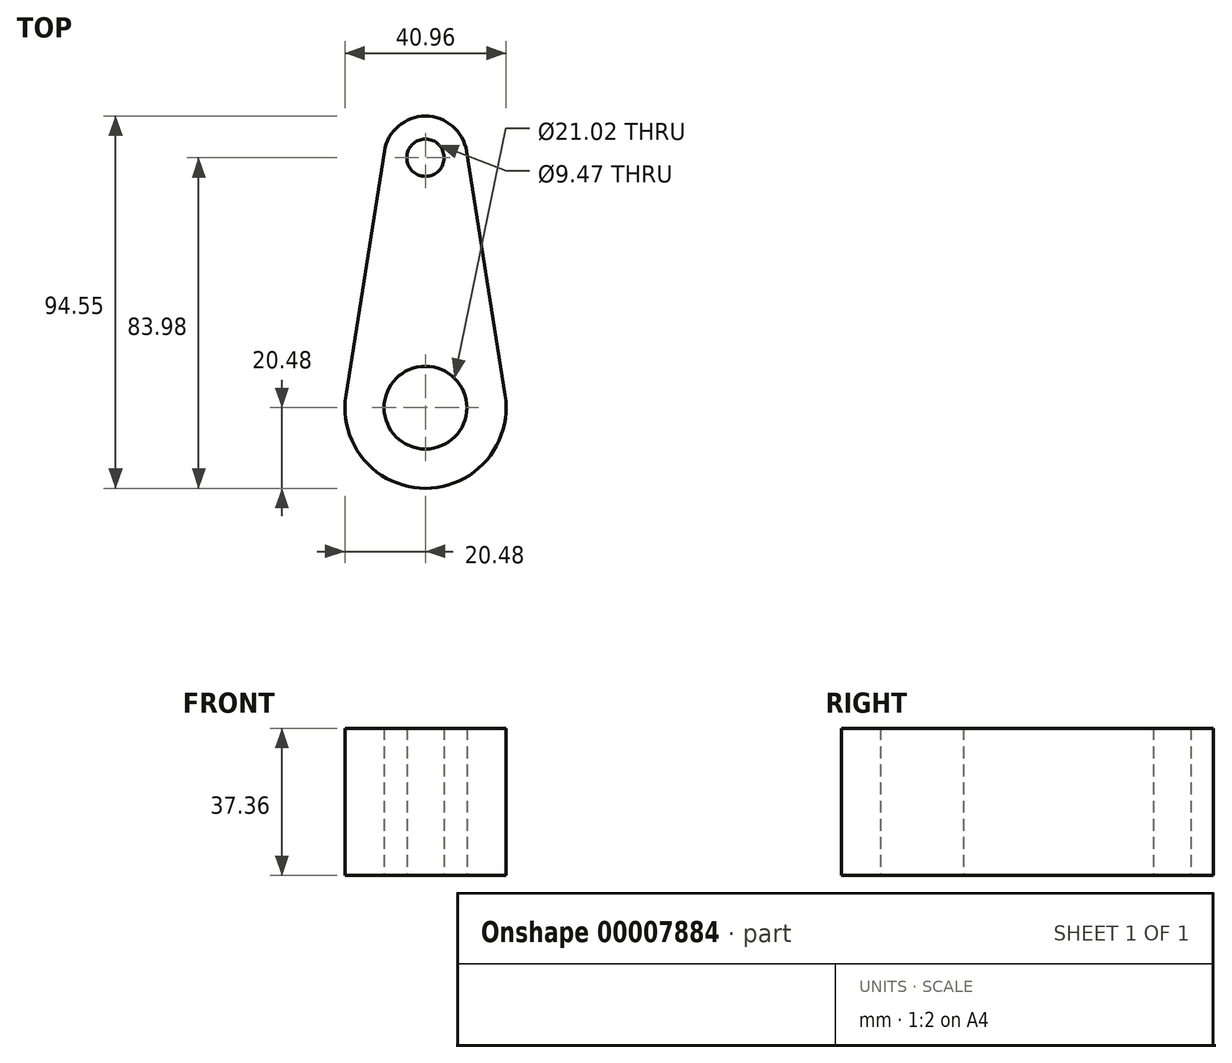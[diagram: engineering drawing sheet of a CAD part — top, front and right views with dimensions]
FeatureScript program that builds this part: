
annotation { "Feature Type Name" : "Feature", "Feature Type Description" : "" }
export const myFeature = defineFeature(function(context is Context, id is Id, definition is map)
    precondition{}
    {
        {
            var Q0;
            Q0=qCreatedBy(makeId("Top.planeOp"),FACE);
            var sketch = newSketch(context, id + "F0", { "sketchPlane" : qUnion([Q0])});
            skCircle(sketch, "E0", {"center": v(0, 0) * mm, "radius": 20.48 * mm});
            skCircle(sketch, "E1", {"center": v(0, 0) * mm, "radius": 10.51 * mm});
            skCircle(sketch, "E2", {"center": v(0, 63.5) * mm, "radius": 10.57 * mm});
            skCircle(sketch, "E3", {"center": v(0, 63.5) * mm, "radius": 4.73 * mm});
            skLineSegment(sketch, "E4", {"start": v(-20.23, 3.2) * mm, "end": v(-10.44, 65.15) * mm});
            skLineSegment(sketch, "E5", {"start": v(20.23, 3.2) * mm, "end": v(10.44, 65.15) * mm});
            skSolve(sketch);
        }
        {
            var Q0;
            Q0 = qSketchRegion(id + "F0", true);
            extrude(context, id + "F1", {"entities" : qUnion([Q0]), "depth" : 37.36 * mm});
        }
    });
